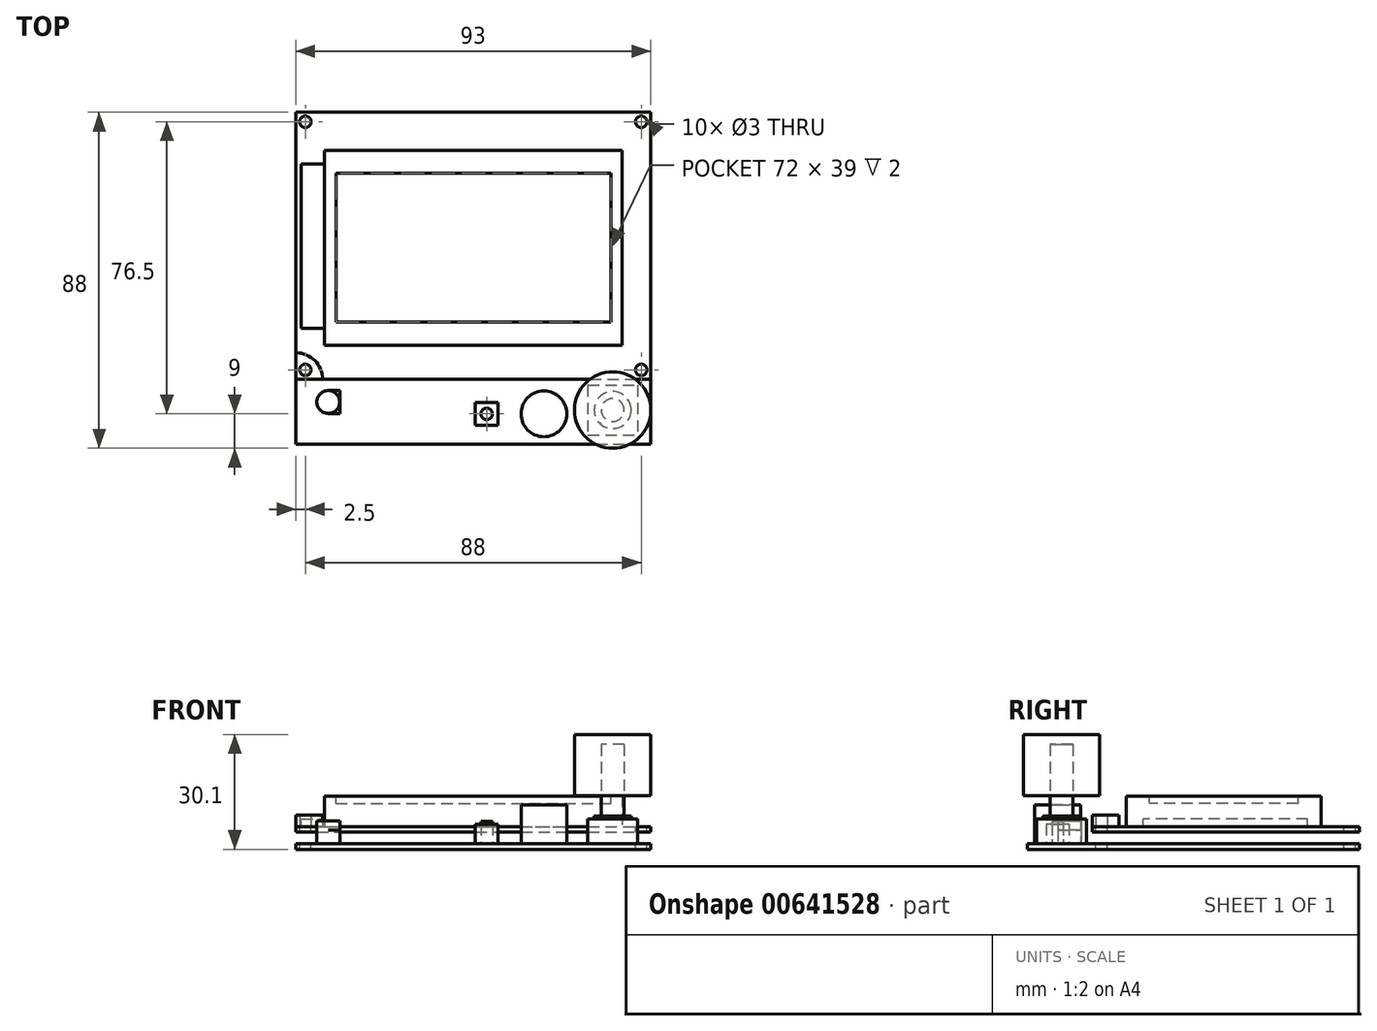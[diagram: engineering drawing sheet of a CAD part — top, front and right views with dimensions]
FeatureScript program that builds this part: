
annotation { "Feature Type Name" : "Feature", "Feature Type Description" : "" }
export const myFeature = defineFeature(function(context is Context, id is Id, definition is map)
    precondition{}
    {
        {
            var Q0;
            Q0=qCreatedBy(makeId("Top.planeOp"),FACE);
            var sketch = newSketch(context, id + "F0", { "sketchPlane" : qUnion([Q0])});
            skLineSegment(sketch, "E0.bottom", {"start": v(-46.5, 43.5) * mm, "end": v(46.5, 43.5) * mm});
            skLineSegment(sketch, "E0.top", {"start": v(-46.5, -43.5) * mm, "end": v(46.5, -43.5) * mm});
            skLineSegment(sketch, "E0.left", {"start": v(-46.5, 43.5) * mm, "end": v(-46.5, -43.5) * mm});
            skLineSegment(sketch, "E0.right", {"start": v(46.5, 43.5) * mm, "end": v(46.5, -43.5) * mm});
            skSolve(sketch);
        }
        {
            var Q0;
            Q0=makeQuery(id+"F0.imprint","IMPRINT",FACE,{"disambiguationData":[TD([[makeQuery(id+"F0.imprint","IMPRINT",EDGE,{"derivedFrom":sQuery(id+"F0.wireOp",EDGE,"E0.bottom")}),-1.0]])]});
            extrude(context, id + "F1", {"entities" : qUnion([Q0]), "depth" : 1.5 * mm, "offsetDistance" : 25 * mm});
        }
        {
            var Q0;
            Q0=makeQuery(id+"F1.opExtrude","CAP_FACE",FACE,{"disambiguationData":[OSD([sQuery(id+"F0.wireOp",EDGE,"E0.bottom"),sQuery(id+"F0.wireOp",EDGE,"E0.top"),sQuery(id+"F0.wireOp",EDGE,"E0.left"),sQuery(id+"F0.wireOp",EDGE,"E0.right")])],"isStart":false});
            cPlane(context, id + "F2", {"entities" : qUnion([Q0]), "cplaneType" : CPlaneType.OFFSET, "offset" : 3 * mm, "width" : 150 * mm, "height" : 150 * mm});
        }
        {
            var Q0;
            Q0=qCreatedBy(id+"F2.planeOp",FACE);
            var sketch = newSketch(context, id + "F3", { "sketchPlane" : qUnion([Q0])});
            skLineSegment(sketch, "E1.0", {"start": v(-46.5, 43.5) * mm, "end": v(46.5, 43.5) * mm});
            skLineSegment(sketch, "E2", {"start": v(-46.5, 43.5) * mm, "end": v(-46.5, -26.5) * mm});
            skLineSegment(sketch, "E3", {"start": v(-46.5, -26.5) * mm, "end": v(46.5, -26.5) * mm});
            skLineSegment(sketch, "E4", {"start": v(46.5, -26.5) * mm, "end": v(46.5, 43.5) * mm});
            skSolve(sketch);
        }
        {
            var Q0;
            Q0=makeQuery(id+"F3.imprint","IMPRINT",FACE,{"disambiguationData":[TD([[makeQuery(id+"F3.imprint","IMPRINT",EDGE,{"derivedFrom":sQuery(id+"F3.wireOp",EDGE,"E1.0")}),-1.0]])]});
            extrude(context, id + "F4", {"entities" : qUnion([Q0]), "depth" : 1.5 * mm, "offsetDistance" : 25 * mm});
        }
        {
            var Q0;
            Q0=makeQuery(id+"F4.opExtrude","CAP_FACE",FACE,{"disambiguationData":[OSD([sQuery(id+"F3.wireOp",EDGE,"E1.0"),sQuery(id+"F3.wireOp",EDGE,"E2"),sQuery(id+"F3.wireOp",EDGE,"E3"),sQuery(id+"F3.wireOp",EDGE,"E4")])],"isStart":false});
            var sketch = newSketch(context, id + "F5", { "sketchPlane" : qUnion([Q0])});
            skLineSegment(sketch, "E5.bottom", {"start": v(-39, 33.5) * mm, "end": v(39, 33.5) * mm});
            skLineSegment(sketch, "E5.top", {"start": v(-39, -17.5) * mm, "end": v(39, -17.5) * mm});
            skLineSegment(sketch, "E5.left", {"start": v(-39, 33.5) * mm, "end": v(-39, -17.5) * mm});
            skLineSegment(sketch, "E5.right", {"start": v(39, 33.5) * mm, "end": v(39, -17.5) * mm});
            skSolve(sketch);
        }
        {
            var Q0;
            Q0=makeQuery(id+"F5.imprint","IMPRINT",FACE,{"disambiguationData":[TD([[makeQuery(id+"F5.imprint","IMPRINT",EDGE,{"derivedFrom":sQuery(id+"F5.wireOp",EDGE,"E5.bottom")}),-1.0]])]});
            extrude(context, id + "F6", {"entities" : qUnion([Q0]), "depth" : 8 * mm, "offsetDistance" : 25 * mm});
        }
        {
            var Q0;
            Q0=makeQuery(id+"F6.opExtrude","CAP_FACE",FACE,{"disambiguationData":[OSD([sQuery(id+"F5.wireOp",EDGE,"E5.bottom"),sQuery(id+"F5.wireOp",EDGE,"E5.top"),sQuery(id+"F5.wireOp",EDGE,"E5.left"),sQuery(id+"F5.wireOp",EDGE,"E5.right")])],"isStart":false});
            var sketch = newSketch(context, id + "F7", { "sketchPlane" : qUnion([Q0])});
            skLineSegment(sketch, "E6.bottom", {"start": v(-36, 27.5) * mm, "end": v(36, 27.5) * mm});
            skLineSegment(sketch, "E6.top", {"start": v(-36, -11.5) * mm, "end": v(36, -11.5) * mm});
            skLineSegment(sketch, "E6.left", {"start": v(-36, 27.5) * mm, "end": v(-36, -11.5) * mm});
            skLineSegment(sketch, "E6.right", {"start": v(36, 27.5) * mm, "end": v(36, -11.5) * mm});
            skLineSegment(sketch, "E7", {"start": v(-17.2, 8) * mm, "end": v(-31.57, 8) * mm, "construction": true});
            skPoint(sketch, "E7.startSnap0", {"position": v(-39, 8) * mm});
            skSolve(sketch);
        }
        {
            var Q0;
            Q0=makeQuery(id+"F7.imprint","IMPRINT",FACE,{"disambiguationData":[TD([[makeQuery(id+"F7.imprint","IMPRINT",EDGE,{"derivedFrom":sQuery(id+"F7.wireOp",EDGE,"E6.bottom")}),-1.0]])]});
            extrude(context, id + "F8", {"entities" : qUnion([Q0]), "operationType" : NewBodyOperationType.REMOVE, "oppositeDirection" : true, "depth" : 2 * mm, "offsetDistance" : 25 * mm});
        }
        {
            var Q0;
            Q0=makeQuery(id+"F6.opExtrude","SWEPT_FACE",FACE,{"disambiguationData":[OSD([sQuery(id+"F5.wireOp",EDGE,"E5.left")])]});
            var sketch = newSketch(context, id + "F9", { "sketchPlane" : qUnion([Q0])});
            skLineSegment(sketch, "E8.bottom", {"start": v(-30, 6) * mm, "end": v(13.1, 6) * mm});
            skLineSegment(sketch, "E8.top", {"start": v(-30, 8) * mm, "end": v(13.1, 8) * mm});
            skLineSegment(sketch, "E8.left", {"start": v(-30, 6) * mm, "end": v(-30, 8) * mm});
            skLineSegment(sketch, "E8.right", {"start": v(13.1, 6) * mm, "end": v(13.1, 8) * mm});
            skSolve(sketch);
        }
        {
            var Q0;
            Q0=makeQuery(id+"F9.imprint","IMPRINT",FACE,{"disambiguationData":[TD([[makeQuery(id+"F9.imprint","IMPRINT",EDGE,{"derivedFrom":sQuery(id+"F9.wireOp",EDGE,"E8.bottom")}),1.0]])]});
            extrude(context, id + "F10", {"entities" : qUnion([Q0]), "depth" : 6.1 * mm, "offsetDistance" : 25 * mm});
        }
        {
            var Q0;
            Q0=makeQuery(id+"F4.opExtrude","CAP_FACE",FACE,{"disambiguationData":[OSD([sQuery(id+"F3.wireOp",EDGE,"E1.0"),sQuery(id+"F3.wireOp",EDGE,"E2"),sQuery(id+"F3.wireOp",EDGE,"E3"),sQuery(id+"F3.wireOp",EDGE,"E4")])],"isStart":false});
            var sketch = newSketch(context, id + "F11", { "sketchPlane" : qUnion([Q0])});
            skPoint(sketch, "E9", {"position": v(-44, 41) * mm});
            skPoint(sketch, "E10", {"position": v(44, 41) * mm});
            skPoint(sketch, "E11", {"position": v(44, -24) * mm});
            skPoint(sketch, "E12", {"position": v(-44, -24) * mm});
            skLineSegment(sketch, "E13", {"start": v(-59.96, 8.5) * mm, "end": v(-19.57, 8.5) * mm, "construction": true});
            skPoint(sketch, "E13.startSnap0", {"position": v(-46.5, 8.5) * mm});
            skSolve(sketch);
        }
        {
            var Q0;
            Q0=sQuery(id+"F11.wireOp",VERTEX,"E9");
            var Q1;
            Q1=sQuery(id+"F11.wireOp",VERTEX,"E10");
            var Q2;
            Q2=sQuery(id+"F11.wireOp",VERTEX,"E11");
            var Q3;
            Q3=sQuery(id+"F11.wireOp",VERTEX,"E12");
            var Q4;
            Q4=makeQuery(id+"F1.opExtrude","SWEPT_BODY",BODY,{"disambiguationData":[OSD([sQuery(id+"F0.wireOp",EDGE,"E0.bottom"),sQuery(id+"F0.wireOp",EDGE,"E0.top"),sQuery(id+"F0.wireOp",EDGE,"E0.left"),sQuery(id+"F0.wireOp",EDGE,"E0.right")])]});
            var Q5;
            Q5=makeQuery(id+"F4.opExtrude","SWEPT_BODY",BODY,{"disambiguationData":[OSD([sQuery(id+"F3.wireOp",EDGE,"E1.0"),sQuery(id+"F3.wireOp",EDGE,"E2"),sQuery(id+"F3.wireOp",EDGE,"E3"),sQuery(id+"F3.wireOp",EDGE,"E4")])]});
            hole(context, id + "F12", {"style" : HoleStyle.SIMPLE, "endStyle" : HoleEndStyle.THROUGH, "holeDiameter" : 3 * mm, "majorDiameter" : 5 * mm, "isTappedThrough" : true, "tappedDepth" : 12 * mm, "tapClearance" : 3, "startFromSketch" : true, "locations" : qUnion([Q0, Q1, Q2, Q3]), "scope" : qUnion([Q4, Q5])});
        }
        {
            var Q0;
            Q0=makeQuery(id+"F1.opExtrude","CAP_FACE",FACE,{"disambiguationData":[OSD([sQuery(id+"F0.wireOp",EDGE,"E0.bottom"),sQuery(id+"F0.wireOp",EDGE,"E0.top"),sQuery(id+"F0.wireOp",EDGE,"E0.left"),sQuery(id+"F0.wireOp",EDGE,"E0.right")])],"isStart":false});
            var sketch = newSketch(context, id + "F13", { "sketchPlane" : qUnion([Q0])});
            skCircle(sketch, "E14", {"center": v(-38, -32.4) * mm, "radius": 3 * mm});
            skLineSegment(sketch, "E15.bottom", {"start": v(-38, -29.4) * mm, "end": v(-34.9, -29.4) * mm});
            skLineSegment(sketch, "E15.top", {"start": v(-38, -35.4) * mm, "end": v(-34.9, -35.4) * mm});
            skLineSegment(sketch, "E15.left", {"start": v(-38, -29.4) * mm, "end": v(-38, -35.4) * mm});
            skLineSegment(sketch, "E15.right", {"start": v(-34.9, -29.4) * mm, "end": v(-34.9, -35.4) * mm});
            skCircle(sketch, "E16", {"center": v(3.5, -35.5) * mm, "radius": 1.5 * mm});
            skLineSegment(sketch, "E17", {"start": v(3.5, -31.9) * mm, "end": v(3.5, -40.51) * mm, "construction": true});
            skLineSegment(sketch, "E18.bottom", {"start": v(0.5, -32.5) * mm, "end": v(6.5, -32.5) * mm});
            skLineSegment(sketch, "E18.top", {"start": v(0.5, -38.5) * mm, "end": v(6.5, -38.5) * mm});
            skLineSegment(sketch, "E18.left", {"start": v(0.5, -32.5) * mm, "end": v(0.5, -38.5) * mm});
            skLineSegment(sketch, "E18.right", {"start": v(6.5, -32.5) * mm, "end": v(6.5, -38.5) * mm});
            skLineSegment(sketch, "E19", {"start": v(3.5, -35.5) * mm, "end": v(8.73, -35.5) * mm, "construction": true});
            skCircle(sketch, "E20", {"center": v(18.5, -35.5) * mm, "radius": 6 * mm});
            skCircle(sketch, "E21", {"center": v(36.5, -34.5) * mm, "radius": 10 * mm});
            skLineSegment(sketch, "E22", {"start": v(36.5, -29.24) * mm, "end": v(36.5, -34.5) * mm, "construction": true});
            skLineSegment(sketch, "E23", {"start": v(36.5, -34.5) * mm, "end": v(32.47, -34.5) * mm, "construction": true});
            skLineSegment(sketch, "E24.bottom", {"start": v(30, -28) * mm, "end": v(43, -28) * mm});
            skLineSegment(sketch, "E24.top", {"start": v(30, -41) * mm, "end": v(43, -41) * mm});
            skLineSegment(sketch, "E24.left", {"start": v(30, -28) * mm, "end": v(30, -41) * mm});
            skLineSegment(sketch, "E24.right", {"start": v(43, -28) * mm, "end": v(43, -41) * mm});
            skCircle(sketch, "E25", {"center": v(36.5, -34.5) * mm, "radius": 4.85 * mm});
            skCircle(sketch, "E26", {"center": v(36.5, -34.5) * mm, "radius": 3 * mm});
            skSolve(sketch);
        }
        {
            var Q0;
            {var subQ0=sQuery(id+"F13.wireOp",EDGE,"E15.left");Q0=makeQuery(id+"F13.imprint","IMPRINT",FACE,{"disambiguationData":[TD([[makeQuery(id+"F13.imprint","IMPRINT",EDGE,{"derivedFrom":subQ0}),1.0]])]});}
            var Q1;
            {var subQ1=sQuery(id+"F13.wireOp",EDGE,"E15.bottom");Q1=makeQuery(id+"F13.imprint","IMPRINT",FACE,{"disambiguationData":[TD([[makeQuery(id+"F13.imprint","IMPRINT",EDGE,{"derivedFrom":subQ1}),-1.0]])]});}
            extrude(context, id + "F14", {"entities" : qUnion([Q0, Q1]), "depth" : 3.6 * mm, "offsetDistance" : 25 * mm});
        }
        {
            var Q0;
            {var subQ0=sQuery(id+"F13.wireOp",EDGE,"E15.left");Q0=makeQuery(id+"F13.imprint","IMPRINT",FACE,{"disambiguationData":[TD([[makeQuery(id+"F13.imprint","IMPRINT",EDGE,{"derivedFrom":subQ0}),-1.0]])]});}
            var Q1;
            {var subQ0=sQuery(id+"F13.wireOp",EDGE,"E15.left");Q1=makeQuery(id+"F13.imprint","IMPRINT",FACE,{"disambiguationData":[TD([[makeQuery(id+"F13.imprint","IMPRINT",EDGE,{"derivedFrom":subQ0}),1.0]])]});}
            extrude(context, id + "F15", {"entities" : qUnion([Q0, Q1]), "operationType" : NewBodyOperationType.ADD, "depth" : 6 * mm, "offsetDistance" : 25 * mm});
        }
        {
            var Q0;
            Q0=makeQuery(id+"F13.imprint","IMPRINT",FACE,{"disambiguationData":[TD([[makeQuery(id+"F13.imprint","IMPRINT",EDGE,{"derivedFrom":sQuery(id+"F13.wireOp",EDGE,"E16")}),1.0]])]});
            var Q1;
            Q1=sQuery(id+"F13.wireOp",EDGE,"E16");
            extrude(context, id + "F16", {"entities" : qUnion([Q0]), "surfaceEntities" : qUnion([Q1]), "depth" : 5.8 * mm, "offsetDistance" : 25 * mm});
        }
        {
            var Q0;
            Q0=makeQuery(id+"F13.imprint","IMPRINT",FACE,{"disambiguationData":[TD([[makeQuery(id+"F13.imprint","IMPRINT",EDGE,{"derivedFrom":sQuery(id+"F13.wireOp",EDGE,"E16")}),-1.0]])]});
            extrude(context, id + "F17", {"entities" : qUnion([Q0]), "depth" : 5.1 * mm, "offsetDistance" : 25 * mm});
        }
        {
            var Q0;
            Q0=makeQuery(id+"F13.imprint","IMPRINT",FACE,{"disambiguationData":[TD([[makeQuery(id+"F13.imprint","IMPRINT",EDGE,{"derivedFrom":sQuery(id+"F13.wireOp",EDGE,"E20")}),1.0]])]});
            var Q1;
            Q1=sQuery(id+"F13.wireOp",EDGE,"E20");
            extrude(context, id + "F18", {"entities" : qUnion([Q0]), "surfaceEntities" : qUnion([Q1]), "depth" : 10.1 * mm, "offsetDistance" : 25 * mm});
        }
        {
            var Q0;
            Q0=makeQuery(id+"F13.imprint","IMPRINT",FACE,{"disambiguationData":[TD([[makeQuery(id+"F13.imprint","IMPRINT",EDGE,{"derivedFrom":sQuery(id+"F13.wireOp",EDGE,"E24.bottom")}),-1.0]])]});
            var Q1;
            Q1=makeQuery(id+"F13.imprint","IMPRINT",FACE,{"disambiguationData":[TD([[makeQuery(id+"F13.imprint","IMPRINT",EDGE,{"derivedFrom":sQuery(id+"F13.wireOp",EDGE,"E25")}),1.0]])]});
            var Q2;
            Q2=makeQuery(id+"F13.imprint","IMPRINT",FACE,{"disambiguationData":[TD([[makeQuery(id+"F13.imprint","IMPRINT",EDGE,{"derivedFrom":sQuery(id+"F13.wireOp",EDGE,"E26")}),1.0]])]});
            extrude(context, id + "F19", {"entities" : qUnion([Q0, Q1, Q2]), "depth" : 6.5 * mm, "offsetDistance" : 25 * mm});
        }
        {
            var Q0;
            Q0=makeQuery(id+"F13.imprint","IMPRINT",FACE,{"disambiguationData":[TD([[makeQuery(id+"F13.imprint","IMPRINT",EDGE,{"derivedFrom":sQuery(id+"F13.wireOp",EDGE,"E25")}),1.0]])]});
            var Q1;
            Q1=makeQuery(id+"F13.imprint","IMPRINT",FACE,{"disambiguationData":[TD([[makeQuery(id+"F13.imprint","IMPRINT",EDGE,{"derivedFrom":sQuery(id+"F13.wireOp",EDGE,"E26")}),1.0]])]});
            extrude(context, id + "F20", {"entities" : qUnion([Q0, Q1]), "operationType" : NewBodyOperationType.ADD, "depth" : 7.2 * mm, "offsetDistance" : 25 * mm});
        }
        {
            var Q0;
            Q0=makeQuery(id+"F13.imprint","IMPRINT",FACE,{"disambiguationData":[TD([[makeQuery(id+"F13.imprint","IMPRINT",EDGE,{"derivedFrom":sQuery(id+"F13.wireOp",EDGE,"E26")}),1.0]])]});
            extrude(context, id + "F21", {"entities" : qUnion([Q0]), "operationType" : NewBodyOperationType.ADD, "depth" : 26 * mm, "offsetDistance" : 25 * mm});
        }
        {
            var Q0;
            {var subQ10=sQuery(id+"F13.wireOp",EDGE,"E15.bottom");Q0=makeQuery(id+"F13.imprint","IMPRINT",FACE,{"disambiguationData":[TD([[makeQuery(id+"F13.imprint","IMPRINT",EDGE,{"derivedFrom":subQ10}),1.0]])]});}
            cPlane(context, id + "F22", {"entities" : qUnion([Q0]), "cplaneType" : CPlaneType.OFFSET, "offset" : 12.6 * mm, "width" : 150 * mm, "height" : 150 * mm});
        }
        {
            var Q0;
            Q0=qCreatedBy(id+"F22.planeOp",FACE);
            var sketch = newSketch(context, id + "F23", { "sketchPlane" : qUnion([Q0])});
            skCircle(sketch, "E27.0", {"center": v(36.5, -34.5) * mm, "radius": 10 * mm});
            skSolve(sketch);
        }
        {
            var Q0;
            Q0=makeQuery(id+"F23.imprint","IMPRINT",FACE,{"disambiguationData":[TD([[makeQuery(id+"F23.imprint","IMPRINT",EDGE,{"derivedFrom":sQuery(id+"F23.wireOp",EDGE,"E27.0")}),1.0]])]});
            extrude(context, id + "F24", {"entities" : qUnion([Q0]), "depth" : 16 * mm, "offsetDistance" : 25 * mm});
        }
        {
            var Q0;
            Q0=makeQuery(id+"F4.opExtrude","CAP_FACE",FACE,{"disambiguationData":[OSD([sQuery(id+"F3.wireOp",EDGE,"E1.0"),sQuery(id+"F3.wireOp",EDGE,"E2"),sQuery(id+"F3.wireOp",EDGE,"E3"),sQuery(id+"F3.wireOp",EDGE,"E4")])],"isStart":false});
            var sketch = newSketch(context, id + "F25", { "sketchPlane" : qUnion([Q0])});
            skLineSegment(sketch, "E28.0", {"start": v(-46.5, -26.5) * mm, "end": v(-39.5, -26.5) * mm});
            skLineSegment(sketch, "E28.1", {"start": v(-46.5, -19.5) * mm, "end": v(-46.5, -26.5) * mm});
            skArc(sketch, "E29", {"start": v(-39.5, -26.5) * mm, "mid": v(-41.55, -21.55) * mm, "end": v(-46.5, -19.5) * mm});
            skPoint(sketch, "E30.orphan", {"position": v(-46.5, 43.5) * mm});
            skPoint(sketch, "E31.orphan", {"position": v(46.5, -26.5) * mm});
            skSolve(sketch);
        }
        {
            var Q0;
            Q0=makeQuery(id+"F25.imprint","IMPRINT",FACE,{"disambiguationData":[TD([[makeQuery(id+"F25.imprint","IMPRINT",EDGE,{"derivedFrom":sQuery(id+"F25.wireOp",EDGE,"E28.0")}),1.0]])]});
            extrude(context, id + "F26", {"entities" : qUnion([Q0]), "depth" : 3 * mm, "offsetDistance" : 25 * mm});
        }
    });
